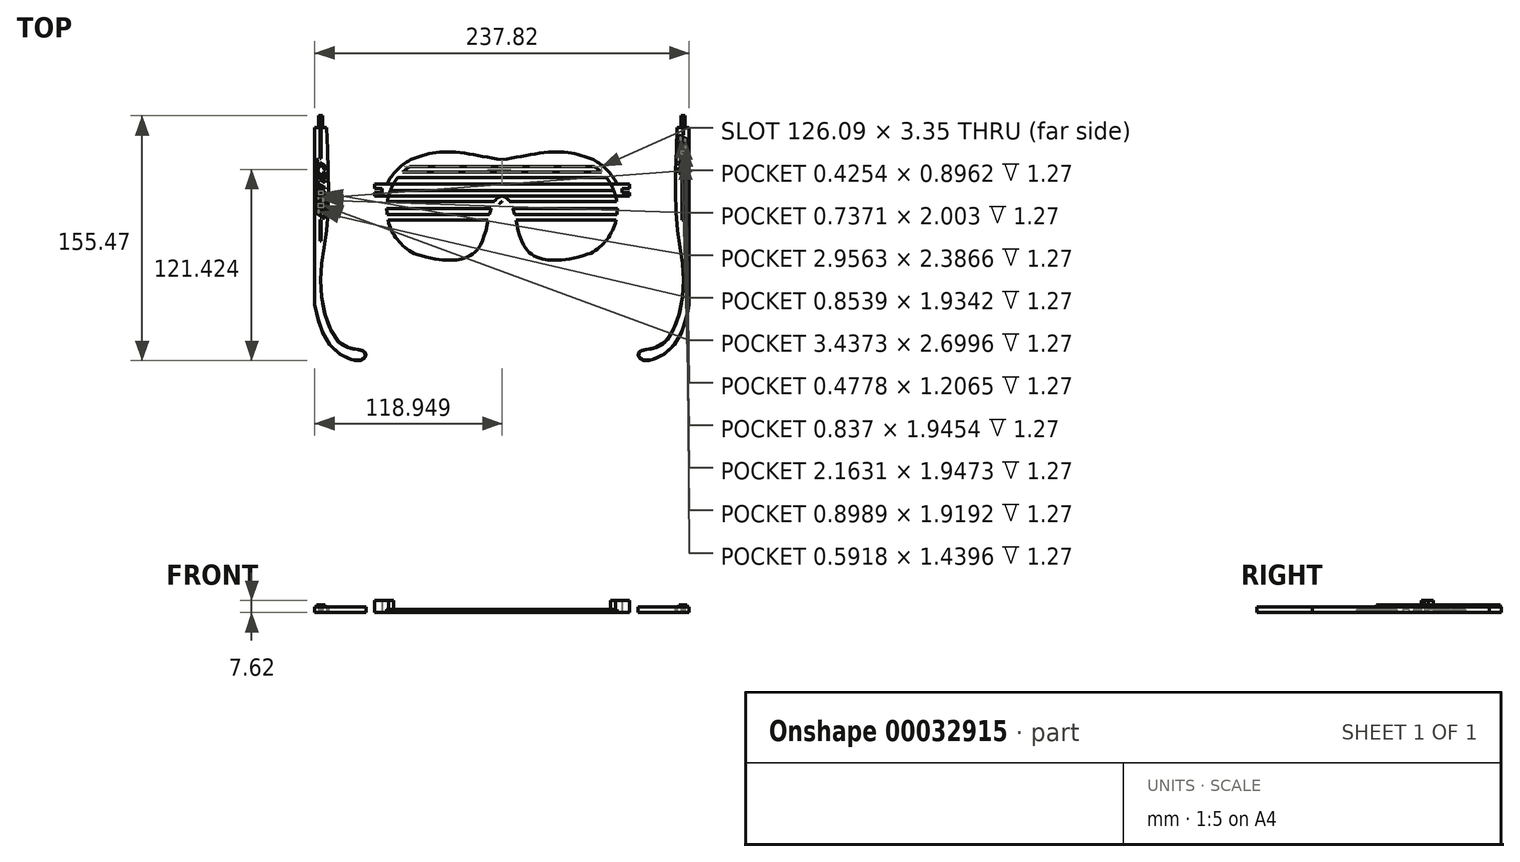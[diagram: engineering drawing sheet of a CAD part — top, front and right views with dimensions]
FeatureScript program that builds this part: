
annotation { "Feature Type Name" : "Feature", "Feature Type Description" : "" }
export const myFeature = defineFeature(function(context is Context, id is Id, definition is map)
    precondition{}
    {
        {
            var Q0;
            Q0=qCreatedBy(makeId("Top.planeOp"),FACE);
            var sketch = newSketch(context, id + "F0", { "sketchPlane" : qUnion([Q0])});
            skArc(sketch, "E0", {"start": v(-58.18, 23.09) * mm, "mid": v(-66.75, 16.58) * mm, "end": v(-72.97, 7.79) * mm});
            skFitSpline(sketch, "E1", {"points": [v(-57.43, -39.6) * mm, v(-39.44, -43.85) * mm, v(-13.97, -37.35) * mm, v(-3.73, -9.63) * mm, v(0, -3.56) * mm], "startDerivative": vector(65.92, -21.2) * mm, "endDerivative": vector(30.4, 18.63) * mm});
            skPoint(sketch, "E2.end.orphan", {"position": v(0, 23.09) * mm});
            skFitSpline(sketch, "E3", {"points": [v(-58.18, 23.09) * mm, v(-37.45, 28.08) * mm, v(0, 23.09) * mm], "startDerivative": vector(44.62, 16.02) * mm, "endDerivative": vector(71, -11.96) * mm});
            skFitSpline(sketch, "E4.3", {"points": [v(-56.35, -36.25) * mm, v(-54.97, -36.7) * mm, v(-52.25, -37.57) * mm, v(-48.08, -38.77) * mm, v(-44.4, -39.6) * mm, v(-41.23, -40.1) * mm, v(-38.72, -40.4) * mm, v(-36.07, -40.59) * mm, v(-32.45, -40.66) * mm, v(-27.87, -40.34) * mm, v(-23.61, -39.32) * mm, v(-20.6, -38.03) * mm, v(-18.93, -37.02) * mm, v(-17.7, -36.07) * mm, v(-16.86, -35.3) * mm, v(-16.07, -34.45) * mm, v(-15.07, -33.16) * mm, v(-13.9, -31.3) * mm, v(-12.26, -27.9) * mm, v(-10.6, -23.01) * mm, v(-9.35, -17.93) * mm, v(-8.48, -14.07) * mm, v(-7.85, -11.35) * mm, v(-7.31, -9.28) * mm, v(-6.84, -7.75) * mm, v(-6.33, -6.34) * mm, v(-5.63, -4.75) * mm, v(-4.6, -3.07) * mm, v(-3.35, -1.63) * mm, v(-2.35, -0.87) * mm, v(-1.84, -0.56) * mm]});
            skArc(sketch, "E4.4", {"start": v(-56.62, 19.9) * mm, "mid": v(-73.17, -8.43) * mm, "end": v(-55.97, -36.37) * mm});
            skFitSpline(sketch, "E4.5", {"points": [v(-56.99, 19.77) * mm, v(-55.12, 20.44) * mm, v(-51.46, 21.77) * mm, v(-46.85, 23.15) * mm, v(-43.01, 23.97) * mm, v(-40.53, 24.33) * mm, v(-38.46, 24.5) * mm, v(-36.34, 24.62) * mm, v(-33.53, 24.6) * mm, v(-29.93, 24.38) * mm, v(-24.87, 23.84) * mm, v(-18.1, 22.8) * mm, v(-9.51, 21.2) * mm, v(-3.58, 20.12) * mm, v(-0.58, 19.62) * mm]});
            skLineSegment(sketch, "E5", {"start": v(-1.84, -0.56) * mm, "end": v(0, 0) * mm});
            skArc(sketch, "E6.MirrorCS", {"start": v(56.74, 19.9) * mm, "mid": v(73.22, -8.43) * mm, "end": v(56.09, -36.37) * mm});
            skArc(sketch, "E7.MirrorCS", {"start": v(58.18, 23.09) * mm, "mid": v(66.75, 16.58) * mm, "end": v(72.97, 7.79) * mm});
            skFitSpline(sketch, "E8.MirrorCS", {"points": [v(57.43, -39.6) * mm, v(39.44, -43.85) * mm, v(13.97, -37.35) * mm, v(3.73, -9.63) * mm, v(0, -3.56) * mm], "startDerivative": vector(-65.92, -21.2) * mm, "endDerivative": vector(-30.4, 18.63) * mm});
            skFitSpline(sketch, "E9.MirrorCS", {"points": [v(56.35, -36.26) * mm, v(54.98, -36.7) * mm, v(52.25, -37.59) * mm, v(48.08, -38.79) * mm, v(44.4, -39.61) * mm, v(41.23, -40.12) * mm, v(38.72, -40.41) * mm, v(36.08, -40.6) * mm, v(32.45, -40.68) * mm, v(27.87, -40.36) * mm, v(23.62, -39.34) * mm, v(20.61, -38.04) * mm, v(18.93, -37.03) * mm, v(17.71, -36.09) * mm, v(16.86, -35.31) * mm, v(16.08, -34.46) * mm, v(15.07, -33.18) * mm, v(13.9, -31.32) * mm, v(12.26, -27.9) * mm, v(10.6, -23.03) * mm, v(9.36, -17.94) * mm, v(8.49, -14.08) * mm, v(7.86, -11.37) * mm, v(7.32, -9.3) * mm, v(6.84, -7.77) * mm, v(6.34, -6.36) * mm, v(5.63, -4.76) * mm, v(4.61, -3.08) * mm, v(3.35, -1.64) * mm, v(2.36, -0.89) * mm, v(1.84, -0.57) * mm]});
            skFitSpline(sketch, "E10.MirrorCS", {"points": [v(58.18, 23.09) * mm, v(37.45, 28.08) * mm, v(0, 23.09) * mm], "startDerivative": vector(-44.62, 16.02) * mm, "endDerivative": vector(-71, -11.96) * mm});
            skFitSpline(sketch, "E11.MirrorCS", {"points": [v(56.99, 19.78) * mm, v(55.12, 20.45) * mm, v(51.45, 21.78) * mm, v(46.85, 23.16) * mm, v(43.01, 23.97) * mm, v(40.52, 24.33) * mm, v(38.46, 24.52) * mm, v(36.34, 24.63) * mm, v(33.53, 24.61) * mm, v(29.93, 24.4) * mm, v(24.87, 23.85) * mm, v(18.1, 22.8) * mm, v(9.5, 21.22) * mm, v(3.57, 20.13) * mm, v(0.58, 19.62) * mm]});
            skLineSegment(sketch, "E12.MirrorCS", {"start": v(1.84, -0.56) * mm, "end": v(0, 0) * mm});
            skLineSegment(sketch, "E13", {"start": v(-0.58, 19.62) * mm, "end": v(0.58, 19.62) * mm});
            skFitSpline(sketch, "E14", {"points": [v(-3.73, -9.63) * mm, v(0, -3.56) * mm, v(3.73, -9.63) * mm], "startDerivative": vector(7.46, 18.21) * mm, "endDerivative": vector(7.46, -18.21) * mm});
            skLineSegment(sketch, "E15", {"start": v(0, 0) * mm, "end": v(72.2, 0) * mm});
            skLineSegment(sketch, "E16", {"start": v(0, 0) * mm, "end": v(-72.14, 0) * mm});
            skLineSegment(sketch, "E17", {"start": v(-71.03, 3.44) * mm, "end": v(71.08, 3.44) * mm});
            skLineSegment(sketch, "E18", {"start": v(-68.96, 7.79) * mm, "end": v(69.02, 7.79) * mm});
            skLineSegment(sketch, "E19", {"start": v(66.43, 11.64) * mm, "end": v(-66.36, 11.64) * mm});
            skLineSegment(sketch, "E20", {"start": v(-63, 15.29) * mm, "end": v(63.09, 15.29) * mm});
            skLineSegment(sketch, "E21", {"start": v(-58.73, 18.64) * mm, "end": v(58.83, 18.64) * mm});
            skLineSegment(sketch, "E22", {"start": v(-52.46, 21.38) * mm, "end": v(-10.42, 21.38) * mm});
            skLineSegment(sketch, "E23.trimOffspring", {"start": v(10.37, 21.38) * mm, "end": v(52.48, 21.38) * mm});
            skLineSegment(sketch, "E24.MirrorCS", {"start": v(-71.03, -3.44) * mm, "end": v(-4.8, -3.44) * mm});
            skLineSegment(sketch, "E25.MirrorCS", {"start": v(-68.96, -7.79) * mm, "end": v(-6.84, -7.79) * mm});
            skLineSegment(sketch, "E26.MirrorCS", {"start": v(-63, -15.29) * mm, "end": v(-8.76, -15.29) * mm});
            skLineSegment(sketch, "E27.MirrorCS", {"start": v(-58.73, -18.64) * mm, "end": v(-9.54, -18.64) * mm});
            skLineSegment(sketch, "E28.MirrorCS", {"start": v(-52.46, -21.38) * mm, "end": v(-10.42, -21.38) * mm});
            skLineSegment(sketch, "E29.MirrorCS", {"start": v(10.37, -21.38) * mm, "end": v(52.48, -21.38) * mm});
            skLineSegment(sketch, "E30.trimOffspring", {"start": v(-7.9, -11.64) * mm, "end": v(-66.36, -11.64) * mm});
            skLineSegment(sketch, "E31.trimOffspring", {"start": v(8.76, -15.29) * mm, "end": v(63.09, -15.29) * mm});
            skLineSegment(sketch, "E32.trimOffspring", {"start": v(9.54, -18.64) * mm, "end": v(58.83, -18.64) * mm});
            skLineSegment(sketch, "E33.trimOffspring", {"start": v(6.84, -7.79) * mm, "end": v(69.02, -7.79) * mm});
            skLineSegment(sketch, "E34", {"start": v(-71.03, -3.44) * mm, "end": v(-72.84, -3.44) * mm});
            skLineSegment(sketch, "E35", {"start": v(-68.96, -7.79) * mm, "end": v(-73.17, -7.79) * mm});
            skLineSegment(sketch, "E36", {"start": v(-66.36, -11.64) * mm, "end": v(-72.97, -11.64) * mm});
            skLineSegment(sketch, "E37", {"start": v(-63, -15.29) * mm, "end": v(-72.34, -15.29) * mm});
            skLineSegment(sketch, "E38", {"start": v(-58.73, -18.64) * mm, "end": v(-71.37, -18.64) * mm});
            skLineSegment(sketch, "E39", {"start": v(-52.46, -21.38) * mm, "end": v(-70.26, -21.38) * mm});
            skLineSegment(sketch, "E40.MirrorCS", {"start": v(52.46, -21.38) * mm, "end": v(70.28, -21.38) * mm});
            skLineSegment(sketch, "E41.MirrorCS", {"start": v(58.76, -18.64) * mm, "end": v(71.39, -18.64) * mm});
            skLineSegment(sketch, "E42.MirrorCS", {"start": v(63.03, -15.29) * mm, "end": v(72.36, -15.29) * mm});
            skLineSegment(sketch, "E43.MirrorCS", {"start": v(68.98, -7.79) * mm, "end": v(73.19, -7.79) * mm});
            skLineSegment(sketch, "E44", {"start": v(-66.3, -27.83) * mm, "end": v(-12.33, -27.83) * mm});
            skLineSegment(sketch, "E45", {"start": v(-62.82, -31.58) * mm, "end": v(-14.11, -31.58) * mm});
            skLineSegment(sketch, "E46", {"start": v(-58.53, -34.89) * mm, "end": v(-16.49, -34.89) * mm});
            skLineSegment(sketch, "E47", {"start": v(-50.85, -37.97) * mm, "end": v(-20.6, -37.97) * mm});
            skLineSegment(sketch, "E48.trimOffspring", {"start": v(11.17, -24.56) * mm, "end": v(68.65, -24.54) * mm});
            skLineSegment(sketch, "E49.trimOffspring", {"start": v(12.33, -27.83) * mm, "end": v(66.37, -27.83) * mm});
            skLineSegment(sketch, "E50.trimOffspring", {"start": v(14.1, -31.58) * mm, "end": v(62.9, -31.58) * mm});
            skLineSegment(sketch, "E51.trimOffspring", {"start": v(16.48, -34.89) * mm, "end": v(58.62, -34.89) * mm});
            skLineSegment(sketch, "E52.trimOffspring", {"start": v(20.58, -37.97) * mm, "end": v(50.9, -37.97) * mm});
            skLineSegment(sketch, "E53.trimOffspring", {"start": v(-11.17, -24.56) * mm, "end": v(-68.58, -24.56) * mm});
            skLineSegment(sketch, "E54", {"start": v(-10.42, -21.38) * mm, "end": v(-10.24, -21.38) * mm});
            skLineSegment(sketch, "E55", {"start": v(10.37, 21.38) * mm, "end": v(10.35, 21.38) * mm});
            skLineSegment(sketch, "E56", {"start": v(-10.42, 21.38) * mm, "end": v(-10.4, 21.38) * mm});
            skLineSegment(sketch, "E57", {"start": v(56.07, -36.36) * mm, "end": v(56.09, -36.37) * mm});
            skLineSegment(sketch, "E58", {"start": v(10.37, -21.38) * mm, "end": v(10.24, -21.38) * mm});
            skLineSegment(sketch, "E59", {"start": v(7.91, -11.64) * mm, "end": v(7.9, -11.64) * mm});
            skLineSegment(sketch, "E60", {"start": v(6.84, -7.79) * mm, "end": v(6.82, -7.79) * mm});
            skLineSegment(sketch, "E61", {"start": v(4.8, -3.44) * mm, "end": v(4.78, -3.44) * mm});
            skLineSegment(sketch, "E62", {"start": v(70.28, -21.38) * mm, "end": v(70.34, -21.38) * mm});
            skLineSegment(sketch, "E63", {"start": v(71.39, -18.64) * mm, "end": v(71.43, -18.64) * mm});
            skLineSegment(sketch, "E64", {"start": v(72.36, -15.29) * mm, "end": v(72.41, -15.29) * mm});
            skLineSegment(sketch, "E65", {"start": v(73, -11.63) * mm, "end": v(73, -11.63) * mm});
            skLineSegment(sketch, "E66", {"start": v(73.19, -7.79) * mm, "end": v(73.24, -7.79) * mm});
            skLineSegment(sketch, "E67", {"start": v(66.43, -11.64) * mm, "end": v(66.4, -11.63) * mm});
            skLineSegment(sketch, "E68", {"start": v(56.73, 19.88) * mm, "end": v(56.74, 19.9) * mm});
            skLineSegment(sketch, "E69", {"start": v(1.84, -0.56) * mm, "end": v(1.84, -0.57) * mm});
            skLineSegment(sketch, "E70", {"start": v(71.05, -3.43) * mm, "end": v(71.08, -3.44) * mm});
            skLineSegment(sketch, "E71", {"start": v(8.76, -15.29) * mm, "end": v(8.75, -15.29) * mm});
            skLineSegment(sketch, "E72", {"start": v(72.85, -3.43) * mm, "end": v(72.86, -3.43) * mm});
            skLineSegment(sketch, "E73", {"start": v(4.8, -3.44) * mm, "end": v(72.89, -3.43) * mm});
            skPoint(sketch, "E74", {"position": v(72.86, -3.43) * mm});
            skPoint(sketch, "E75.trimOffspring.end.orphan", {"position": v(83.8, -3.43) * mm});
            skLineSegment(sketch, "E76", {"start": v(7.91, -11.64) * mm, "end": v(73.02, -11.64) * mm});
            skPoint(sketch, "E77", {"position": v(73, -11.63) * mm});
            skLineSegment(sketch, "E78", {"start": v(-75.78, 0) * mm, "end": v(-81.03, 0) * mm});
            skLineSegment(sketch, "E79", {"start": v(-72.97, 7.79) * mm, "end": v(-81.03, 7.79) * mm});
            skLineSegment(sketch, "E80", {"start": v(75.78, 0) * mm, "end": v(81.08, 0) * mm});
            skLineSegment(sketch, "E81", {"start": v(72.97, 7.79) * mm, "end": v(81.08, 7.79) * mm});
            skLineSegment(sketch, "E82", {"start": v(81.08, 7.79) * mm, "end": v(81.08, 4.74) * mm});
            skLineSegment(sketch, "E83", {"start": v(-81.03, 0) * mm, "end": v(-81.03, 2.2) * mm});
            skLineSegment(sketch, "E84.rect.bottom", {"start": v(-76.1, 2.2) * mm, "end": v(-81.03, 2.2) * mm});
            skLineSegment(sketch, "E84.rect.top", {"start": v(-76.1, 4.74) * mm, "end": v(-81.03, 4.74) * mm});
            skLineSegment(sketch, "E84.rect.left", {"start": v(-76.1, 2.2) * mm, "end": v(-76.1, 4.74) * mm});
            skPoint(sketch, "E84.rect.middle", {"position": v(-81.03, 3.9) * mm});
            skLineSegment(sketch, "E85.trimOffspring", {"start": v(-81.03, 4.74) * mm, "end": v(-81.03, 7.79) * mm});
            skPoint(sketch, "E86.startSnap0", {"position": v(0.04, 15.29) * mm});
            skLineSegment(sketch, "E87.MirrorCS", {"start": v(76.18, 4.74) * mm, "end": v(81.1, 4.74) * mm});
            skLineSegment(sketch, "E88.MirrorCS", {"start": v(76.18, 2.2) * mm, "end": v(76.18, 4.74) * mm});
            skLineSegment(sketch, "E89.MirrorCS", {"start": v(76.18, 2.2) * mm, "end": v(81.1, 2.2) * mm});
            skLineSegment(sketch, "E90.trimOffspring", {"start": v(81.08, 2.2) * mm, "end": v(81.08, 0) * mm});
            skArc(sketch, "E91.trimOffspring", {"start": v(-75.78, 0) * mm, "mid": v(-73.43, -22.96) * mm, "end": v(-57.43, -39.6) * mm});
            skArc(sketch, "E92.trimOffspring", {"start": v(75.78, 0) * mm, "mid": v(73.43, -22.96) * mm, "end": v(57.43, -39.6) * mm});
            skLineSegment(sketch, "E93", {"start": v(-72.97, 7.79) * mm, "end": v(-68.96, 7.79) * mm});
            skLineSegment(sketch, "E94", {"start": v(-75.78, 0) * mm, "end": v(-72.14, 0) * mm});
            skLineSegment(sketch, "E95", {"start": v(75.78, 0) * mm, "end": v(72.2, 0) * mm});
            skLineSegment(sketch, "E96", {"start": v(72.97, 7.79) * mm, "end": v(69.02, 7.79) * mm});
            skSolve(sketch);
        }
        {
            var Q0;
            Q0=makeQuery(id+"F0.imprint","IMPRINT",FACE,{"disambiguationData":[TD([[makeQuery(id+"F0.imprint","IMPRINT",EDGE,{"derivedFrom":sQuery(id+"F0.wireOp",EDGE,"E0")}),1.0]])]});
            var Q1;
            {var subQ1=sQuery(id+"F0.wireOp",EDGE,"E19");Q1=makeQuery(id+"F0.imprint","IMPRINT",FACE,{"disambiguationData":[TD([[makeQuery(id+"F0.imprint","IMPRINT",EDGE,{"derivedFrom":subQ1}),-1.0]])]});}
            var Q2;
            {var subQ2=sQuery(id+"F0.wireOp",EDGE,"E13");Q2=makeQuery(id+"F0.imprint","IMPRINT",FACE,{"disambiguationData":[TD([[makeQuery(id+"F0.imprint","IMPRINT",EDGE,{"derivedFrom":subQ2}),-1.0]])]});}
            var Q3;
            {var subQ1=sQuery(id+"F0.wireOp",EDGE,"E17");Q3=makeQuery(id+"F0.imprint","IMPRINT",FACE,{"disambiguationData":[TD([[makeQuery(id+"F0.imprint","IMPRINT",EDGE,{"derivedFrom":subQ1}),1.0]])]});}
            var Q4;
            {var subQ3=sQuery(id+"F0.wireOp",EDGE,"E5");Q4=makeQuery(id+"F0.imprint","IMPRINT",FACE,{"disambiguationData":[TD([[makeQuery(id+"F0.imprint","IMPRINT",EDGE,{"derivedFrom":subQ3}),1.0]])]});}
            var Q5;
            Q5=makeQuery(id+"F0.imprint","IMPRINT",FACE,{"disambiguationData":[TD([[makeQuery(id+"F0.imprint","IMPRINT",EDGE,{"derivedFrom":sQuery(id+"F0.wireOp",EDGE,"E12.MirrorCS")}),-1.0]])]});
            var Q6;
            {var subQ11=sQuery(id+"F0.wireOp",EDGE,"E33.trimOffspring");Q6=makeQuery(id+"F0.imprint","IMPRINT",FACE,{"disambiguationData":[TD([[makeQuery(id+"F0.imprint","IMPRINT",EDGE,{"derivedFrom":subQ11}),-1.0]])]});}
            var Q7;
            {var subQ2=sQuery(id+"F0.wireOp",EDGE,"E25.MirrorCS");Q7=makeQuery(id+"F0.imprint","IMPRINT",FACE,{"disambiguationData":[TD([[makeQuery(id+"F0.imprint","IMPRINT",EDGE,{"derivedFrom":subQ2}),-1.0]])]});}
            var Q8;
            {var subQ3=sQuery(id+"F0.wireOp",EDGE,"E26.MirrorCS");Q8=makeQuery(id+"F0.imprint","IMPRINT",FACE,{"disambiguationData":[TD([[makeQuery(id+"F0.imprint","IMPRINT",EDGE,{"derivedFrom":subQ3}),-1.0]])]});}
            var Q9;
            {var subQ10=sQuery(id+"F0.wireOp",EDGE,"E31.trimOffspring");Q9=makeQuery(id+"F0.imprint","IMPRINT",FACE,{"disambiguationData":[TD([[makeQuery(id+"F0.imprint","IMPRINT",EDGE,{"derivedFrom":subQ10}),-1.0]])]});}
            var Q10;
            {var subQ7=sQuery(id+"F0.wireOp",EDGE,"E29.MirrorCS");Q10=makeQuery(id+"F0.imprint","IMPRINT",FACE,{"disambiguationData":[TD([[makeQuery(id+"F0.imprint","IMPRINT",EDGE,{"derivedFrom":subQ7}),-1.0]])]});}
            var Q11;
            Q11=makeQuery(id+"F0.imprint","IMPRINT",FACE,{"disambiguationData":[TD([[makeQuery(id+"F0.imprint","IMPRINT",EDGE,{"derivedFrom":sQuery(id+"F0.wireOp",EDGE,"E28.MirrorCS")}),-1.0]])]});
            var Q12;
            {var subQ1=sQuery(id+"F0.wireOp",EDGE,"E44");Q12=makeQuery(id+"F0.imprint","IMPRINT",FACE,{"disambiguationData":[TD([[makeQuery(id+"F0.imprint","IMPRINT",EDGE,{"derivedFrom":subQ1}),-1.0]])]});}
            var Q13;
            {var subQ1=sQuery(id+"F0.wireOp",EDGE,"E49.trimOffspring");Q13=makeQuery(id+"F0.imprint","IMPRINT",FACE,{"disambiguationData":[TD([[makeQuery(id+"F0.imprint","IMPRINT",EDGE,{"derivedFrom":subQ1}),-1.0]])]});}
            var Q14;
            {var subQ2=sQuery(id+"F0.wireOp",EDGE,"E51.trimOffspring");Q14=makeQuery(id+"F0.imprint","IMPRINT",FACE,{"disambiguationData":[TD([[makeQuery(id+"F0.imprint","IMPRINT",EDGE,{"derivedFrom":subQ2}),-1.0]])]});}
            var Q15;
            {var subQ1=sQuery(id+"F0.wireOp",EDGE,"E46");Q15=makeQuery(id+"F0.imprint","IMPRINT",FACE,{"disambiguationData":[TD([[makeQuery(id+"F0.imprint","IMPRINT",EDGE,{"derivedFrom":subQ1}),-1.0]])]});}
            var Q16;
            Q16=makeQuery(id+"F0.imprint","IMPRINT",FACE,{"disambiguationData":[TD([[makeQuery(id+"F0.imprint","IMPRINT",EDGE,{"derivedFrom":sQuery(id+"F0.wireOp",EDGE,"E1")}),1.0]])]});
            var Q17;
            Q17=makeQuery(id+"F0.imprint","IMPRINT",FACE,{"disambiguationData":[TD([[makeQuery(id+"F0.imprint","IMPRINT",EDGE,{"derivedFrom":sQuery(id+"F0.wireOp",EDGE,"E78")}),-1.0]])]});
            var Q18;
            Q18=makeQuery(id+"F0.imprint","IMPRINT",FACE,{"disambiguationData":[TD([[makeQuery(id+"F0.imprint","IMPRINT",EDGE,{"derivedFrom":sQuery(id+"F0.wireOp",EDGE,"E80")}),1.0]])]});
            extrude(context, id + "F1", {"entities" : qUnion([Q0, Q1, Q2, Q3, Q4, Q5, Q6, Q7, Q8, Q9, Q10, Q11, Q12, Q13, Q14, Q15, Q16, Q17, Q18]), "depth" : 1.9 * mm});
        }
        {
            var Q0;
            Q0=qCreatedBy(makeId("Top.planeOp"),FACE);
            var sketch = newSketch(context, id + "F2", { "sketchPlane" : qUnion([Q0])});
            skLineSegment(sketch, "E97", {"start": v(-118.9, 43.4) * mm, "end": v(-118.9, -68.92) * mm});
            skLineSegment(sketch, "E98", {"start": v(-118.9, 43.4) * mm, "end": v(-116.37, 43.4) * mm});
            skPoint(sketch, "E99.2.internal.snap0", {"position": v(-115.1, 43.4) * mm});
            skFitSpline(sketch, "E99", {"points": [v(-111.29, 43.4) * mm, v(-111.29, -19.18) * mm, v(-115.1, -60.4) * mm, v(-101.96, -94.17) * mm, v(-89.37, -97.9) * mm, v(-86.4, -100.45) * mm, v(-89.74, -104.24) * mm, v(-108.09, -95.9) * mm, v(-118.9, -68.92) * mm], "startDerivative": vector(13.53, -320.53) * mm, "endDerivative": vector(-45.53, 212.03) * mm});
            skPoint(sketch, "E100.orphan", {"position": v(-118.9, -83.6) * mm});
            skFitSpline(sketch, "E101.MirrorCS", {"points": [v(111.29, 43.4) * mm, v(111.29, -19.18) * mm, v(115.1, -60.4) * mm, v(101.96, -94.17) * mm, v(89.37, -97.9) * mm, v(86.4, -100.45) * mm, v(89.74, -104.24) * mm, v(108.09, -95.9) * mm, v(118.9, -68.92) * mm], "startDerivative": vector(-13.53, -320.53) * mm, "endDerivative": vector(45.53, 212.03) * mm});
            skLineSegment(sketch, "E102.MirrorCS", {"start": v(118.9, 43.4) * mm, "end": v(118.9, -68.92) * mm});
            skLineSegment(sketch, "E103.MirrorCS", {"start": v(118.9, 43.4) * mm, "end": v(116.37, 43.4) * mm});
            skLineSegment(sketch, "E104.rect.bottom", {"start": v(-116.37, 51.01) * mm, "end": v(-113.83, 51.01) * mm});
            skLineSegment(sketch, "E104.rect.left", {"start": v(-116.37, 51.01) * mm, "end": v(-116.37, 43.4) * mm});
            skLineSegment(sketch, "E104.rect.right", {"start": v(-113.83, 51.01) * mm, "end": v(-113.83, 43.4) * mm});
            skPoint(sketch, "E104.rect.top.end.orphan", {"position": v(-113.83, 35.77) * mm});
            skPoint(sketch, "E105.orphan", {"position": v(-116.37, 35.77) * mm});
            skLineSegment(sketch, "E106.trimOffspring", {"start": v(-113.83, 43.4) * mm, "end": v(-111.29, 43.4) * mm});
            skLineSegment(sketch, "E107.MirrorCS", {"start": v(116.37, 51.01) * mm, "end": v(116.37, 43.4) * mm});
            skLineSegment(sketch, "E108.MirrorCS", {"start": v(116.37, 51.01) * mm, "end": v(113.83, 51.01) * mm});
            skLineSegment(sketch, "E109.MirrorCS", {"start": v(113.83, 51.01) * mm, "end": v(113.83, 43.4) * mm});
            skLineSegment(sketch, "E110.trimOffspring", {"start": v(113.83, 43.4) * mm, "end": v(111.29, 43.4) * mm});
            skSolve(sketch);
        }
        {
            var Q0;
            Q0=makeQuery(id+"F0.imprint","IMPRINT",FACE,{"disambiguationData":[TD([[makeQuery(id+"F0.imprint","IMPRINT",EDGE,{"derivedFrom":sQuery(id+"F0.wireOp",EDGE,"E78")}),-1.0]])]});
            var Q1;
            Q1=makeQuery(id+"F0.imprint","IMPRINT",FACE,{"disambiguationData":[TD([[makeQuery(id+"F0.imprint","IMPRINT",EDGE,{"derivedFrom":sQuery(id+"F0.wireOp",EDGE,"E80")}),1.0]])]});
            extrude(context, id + "F3", {"entities" : qUnion([Q0, Q1]), "operationType" : NewBodyOperationType.ADD, "depth" : 7.62 * mm});
        }
        {
            var Q0;
            Q0=makeQuery(id+"F2.imprint","IMPRINT",FACE,{"disambiguationData":[TD([[makeQuery(id+"F2.imprint","IMPRINT",EDGE,{"derivedFrom":sQuery(id+"F2.wireOp",EDGE,"E97")}),1.0]])]});
            var Q1;
            Q1=makeQuery(id+"F2.imprint","IMPRINT",FACE,{"disambiguationData":[TD([[makeQuery(id+"F2.imprint","IMPRINT",EDGE,{"derivedFrom":sQuery(id+"F2.wireOp",EDGE,"E101.MirrorCS")}),1.0]])]});
            extrude(context, id + "F4", {"entities" : qUnion([Q0, Q1]), "depth" : 4.93 * mm});
        }
        {
            var Q0;
            Q0=makeQuery(id+"F4.opExtrude","CAP_FACE",FACE,{"disambiguationData":[OSD([sQuery(id+"F2.wireOp",EDGE,"E97"),sQuery(id+"F2.wireOp",EDGE,"E98"),sQuery(id+"F2.wireOp",EDGE,"E99"),sQuery(id+"F2.wireOp",EDGE,"E104.rect.bottom"),sQuery(id+"F2.wireOp",EDGE,"E104.rect.left"),sQuery(id+"F2.wireOp",EDGE,"E104.rect.right"),sQuery(id+"F2.wireOp",EDGE,"E106.trimOffspring")])],"isStart":false});
            var sketch = newSketch(context, id + "F5", { "sketchPlane" : qUnion([Q0])});
            skLineSegment(sketch, "E111", {"start": v(-117.84, -10.83) * mm, "end": v(-117.84, -7.26) * mm});
            skLineSegment(sketch, "E112", {"start": v(-112.42, -14.1) * mm, "end": v(-112.42, -11.99) * mm});
            skLineSegment(sketch, "E113", {"start": v(-117.84, -10.83) * mm, "end": v(-112.42, -14.1) * mm});
            skLineSegment(sketch, "E114", {"start": v(-117.84, -7.26) * mm, "end": v(-115.14, -8.88) * mm});
            skLineSegment(sketch, "E115", {"start": v(-115.14, -8.88) * mm, "end": v(-115.14, -10.8) * mm});
            skLineSegment(sketch, "E116", {"start": v(-115.14, -10.8) * mm, "end": v(-112.42, -9) * mm});
            skLineSegment(sketch, "E117", {"start": v(-112.42, -9) * mm, "end": v(-112.42, -10.6) * mm});
            skLineSegment(sketch, "E118", {"start": v(-112.42, -10.6) * mm, "end": v(-113.53, -11.32) * mm});
            skLineSegment(sketch, "E119", {"start": v(-113.53, -11.32) * mm, "end": v(-112.42, -11.99) * mm});
            skLineSegment(sketch, "E120", {"start": v(-112.42, -11.99) * mm, "end": v(-112.42, -14.1) * mm});
            skLineSegment(sketch, "E121", {"start": v(-112.42, -9.01) * mm, "end": v(-117.84, -5.74) * mm});
            skLineSegment(sketch, "E122", {"start": v(-117.84, -5.74) * mm, "end": v(-117.84, -2.81) * mm});
            skLineSegment(sketch, "E123", {"start": v(-117.84, -2.81) * mm, "end": v(-112.42, -6.08) * mm});
            skLineSegment(sketch, "E124", {"start": v(-112.42, -6.08) * mm, "end": v(-112.42, -9.01) * mm});
            skLineSegment(sketch, "E125", {"start": v(-112.42, -5.42) * mm, "end": v(-117.84, -2.15) * mm});
            skLineSegment(sketch, "E126", {"start": v(-117.84, -2.15) * mm, "end": v(-117.84, 0.92) * mm});
            skLineSegment(sketch, "E127", {"start": v(-117.84, 0.92) * mm, "end": v(-115.33, -0.6) * mm});
            skLineSegment(sketch, "E128", {"start": v(-115.33, -0.6) * mm, "end": v(-115.33, -2.21) * mm});
            skLineSegment(sketch, "E129", {"start": v(-115.33, -2.21) * mm, "end": v(-114.94, -2.45) * mm});
            skLineSegment(sketch, "E130", {"start": v(-114.94, -2.45) * mm, "end": v(-114.94, 0) * mm});
            skLineSegment(sketch, "E131", {"start": v(-114.94, 0) * mm, "end": v(-112.42, -1.52) * mm});
            skLineSegment(sketch, "E132", {"start": v(-112.42, -1.52) * mm, "end": v(-112.42, -5.42) * mm});
            skLineSegment(sketch, "E133", {"start": v(-117.84, 2.04) * mm, "end": v(-112.42, -1.22) * mm});
            skLineSegment(sketch, "E134", {"start": v(-112.42, -1.22) * mm, "end": v(-112.42, 1.27) * mm});
            skLineSegment(sketch, "E135", {"start": v(-117.84, 4.54) * mm, "end": v(-117.84, 2.04) * mm});
            skLineSegment(sketch, "E136", {"start": v(-117.84, 5.51) * mm, "end": v(-112.42, 2.25) * mm});
            skLineSegment(sketch, "E137", {"start": v(-112.42, 1.27) * mm, "end": v(-112.42, 2.25) * mm});
            skLineSegment(sketch, "E138", {"start": v(-117.84, 4.54) * mm, "end": v(-117.84, 5.51) * mm});
            skLineSegment(sketch, "E139", {"start": v(-112.42, 4.5) * mm, "end": v(-116.95, 7.23) * mm});
            skLineSegment(sketch, "E140", {"start": v(-116.95, 7.23) * mm, "end": v(-116.95, 5.26) * mm});
            skLineSegment(sketch, "E141", {"start": v(-116.95, 5.26) * mm, "end": v(-117.84, 5.8) * mm});
            skLineSegment(sketch, "E142", {"start": v(-117.84, 5.8) * mm, "end": v(-117.84, 10.32) * mm});
            skLineSegment(sketch, "E143", {"start": v(-116.95, 8.1) * mm, "end": v(-116.95, 9.79) * mm});
            skLineSegment(sketch, "E144", {"start": v(-117.84, 10.32) * mm, "end": v(-116.95, 9.79) * mm});
            skLineSegment(sketch, "E145", {"start": v(-116.95, 8.1) * mm, "end": v(-112.42, 5.38) * mm});
            skLineSegment(sketch, "E146", {"start": v(-112.42, 5.38) * mm, "end": v(-112.42, 4.5) * mm});
            skLineSegment(sketch, "E147", {"start": v(-117.84, 11.14) * mm, "end": v(-116.93, 10.6) * mm});
            skLineSegment(sketch, "E148", {"start": v(-116.93, 10.6) * mm, "end": v(-116.93, 12.55) * mm});
            skLineSegment(sketch, "E149", {"start": v(-116.93, 12.55) * mm, "end": v(-117.84, 13.1) * mm});
            skLineSegment(sketch, "E150", {"start": v(-117.84, 13.1) * mm, "end": v(-117.84, 11.14) * mm});
            skLineSegment(sketch, "E151", {"start": v(-112.42, 9.98) * mm, "end": v(-115.47, 11.82) * mm});
            skLineSegment(sketch, "E152", {"start": v(-112.42, 11.16) * mm, "end": v(-112.42, 10.88) * mm});
            skLineSegment(sketch, "E153", {"start": v(-115.47, 11.82) * mm, "end": v(-115.47, 10.48) * mm});
            skLineSegment(sketch, "E154", {"start": v(-115.47, 10.48) * mm, "end": v(-112.42, 8.64) * mm});
            skLineSegment(sketch, "E155", {"start": v(-112.42, 8.64) * mm, "end": v(-112.42, 9.98) * mm});
            skLineSegment(sketch, "E156", {"start": v(-117.84, 14.15) * mm, "end": v(-112.42, 10.88) * mm});
            skLineSegment(sketch, "E157", {"start": v(-112.42, 10.88) * mm, "end": v(-112.42, 15.19) * mm});
            skLineSegment(sketch, "E158", {"start": v(-112.42, 15.19) * mm, "end": v(-113.17, 15.64) * mm});
            skLineSegment(sketch, "E159", {"start": v(-113.17, 15.64) * mm, "end": v(-113.17, 12.5) * mm});
            skLineSegment(sketch, "E160", {"start": v(-113.17, 12.5) * mm, "end": v(-116.93, 14.76) * mm});
            skLineSegment(sketch, "E161", {"start": v(-117.84, 18.45) * mm, "end": v(-117.84, 14.15) * mm});
            skLineSegment(sketch, "E162", {"start": v(-116.93, 14.76) * mm, "end": v(-116.93, 17.9) * mm});
            skLineSegment(sketch, "E163.trimOffspring", {"start": v(-116.93, 17.9) * mm, "end": v(-117.84, 18.45) * mm});
            skLineSegment(sketch, "E164", {"start": v(-117.84, 19.8) * mm, "end": v(-115.13, 18.18) * mm});
            skLineSegment(sketch, "E165", {"start": v(-113.4, 17.13) * mm, "end": v(-113.4, 19.02) * mm});
            skLineSegment(sketch, "E166", {"start": v(-116.99, 23.09) * mm, "end": v(-117.84, 23.6) * mm});
            skLineSegment(sketch, "E167", {"start": v(-117.84, 23.6) * mm, "end": v(-117.84, 19.8) * mm});
            skLineSegment(sketch, "E168", {"start": v(-116.99, 23.09) * mm, "end": v(-116.99, 20.43) * mm});
            skLineSegment(sketch, "E169", {"start": v(-116.99, 20.43) * mm, "end": v(-115.52, 19.55) * mm});
            skLineSegment(sketch, "E170", {"start": v(-115.52, 19.55) * mm, "end": v(-115.52, 21.36) * mm});
            skLineSegment(sketch, "E171", {"start": v(-115.52, 21.36) * mm, "end": v(-113.4, 20.08) * mm});
            skLineSegment(sketch, "E172", {"start": v(-115.13, 18.18) * mm, "end": v(-115.13, 20.07) * mm});
            skLineSegment(sketch, "E173", {"start": v(-115.13, 20.07) * mm, "end": v(-113.4, 19.02) * mm});
            skLineSegment(sketch, "E174", {"start": v(-113.4, 20.08) * mm, "end": v(-112.42, 19.5) * mm});
            skPoint(sketch, "E175.trimOffspring.end.orphan", {"position": v(-113.4, 20.92) * mm});
            skLineSegment(sketch, "E176.trimOffspring", {"start": v(-113.4, 17.13) * mm, "end": v(-112.42, 16.54) * mm});
            skPoint(sketch, "E177.firstSnap0", {"position": v(-115.52, 20.46) * mm});
            skLineSegment(sketch, "E177.bottom", {"start": v(-115.52, 23.96) * mm, "end": v(-114.84, 23.96) * mm});
            skLineSegment(sketch, "E177.top", {"start": v(-115.52, 50.25) * mm, "end": v(-114.84, 50.25) * mm});
            skLineSegment(sketch, "E177.left", {"start": v(-115.52, 23.96) * mm, "end": v(-115.52, 50.25) * mm});
            skLineSegment(sketch, "E177.right", {"start": v(-114.84, 23.96) * mm, "end": v(-114.84, 50.25) * mm});
            skLineSegment(sketch, "E178.bottom", {"start": v(-114.97, -28.57) * mm, "end": v(-115.56, -28.57) * mm});
            skLineSegment(sketch, "E178.top", {"start": v(-114.97, -14.76) * mm, "end": v(-115.56, -14.76) * mm});
            skLineSegment(sketch, "E178.left", {"start": v(-114.97, -28.57) * mm, "end": v(-114.97, -14.76) * mm});
            skLineSegment(sketch, "E178.right", {"start": v(-115.56, -28.57) * mm, "end": v(-115.56, -14.76) * mm});
            skLineSegment(sketch, "E179.trimOffspring", {"start": v(-112.42, -10.6) * mm, "end": v(-112.42, -6.08) * mm});
            skLineSegment(sketch, "E180.trimOffspring", {"start": v(-117.84, 2.04) * mm, "end": v(-117.84, 4.54) * mm});
            skLineSegment(sketch, "E181.trimOffspring", {"start": v(-117.84, 14.15) * mm, "end": v(-117.84, 18.45) * mm});
            skLineSegment(sketch, "E182.trimOffspring", {"start": v(-117.84, 19.8) * mm, "end": v(-117.84, 23.6) * mm});
            skLineSegment(sketch, "E183.trimOffspring", {"start": v(-112.42, 16.54) * mm, "end": v(-112.42, 19.5) * mm});
            skLineSegment(sketch, "E184.trimOffspring", {"start": v(-112.42, 4.5) * mm, "end": v(-112.42, 5.38) * mm});
            skLineSegment(sketch, "E185.trimOffspring", {"start": v(-112.42, -1.22) * mm, "end": v(-112.42, 2.25) * mm});
            skLineSegment(sketch, "E186.trimOffspring", {"start": v(-112.42, -5.42) * mm, "end": v(-112.42, -1.52) * mm});
            skLineSegment(sketch, "E187.trimOffspring", {"start": v(-117.84, 5.8) * mm, "end": v(-117.84, 13.1) * mm});
            skLineSegment(sketch, "E188.0", {"start": v(-116.85, -4.56) * mm, "end": v(-113.41, -6.63) * mm});
            skLineSegment(sketch, "E188.1", {"start": v(-116.85, -5.19) * mm, "end": v(-116.85, -4.56) * mm});
            skLineSegment(sketch, "E188.2", {"start": v(-113.41, -7.26) * mm, "end": v(-116.85, -5.19) * mm});
            skLineSegment(sketch, "E188.3", {"start": v(-113.41, -6.63) * mm, "end": v(-113.41, -7.26) * mm});
            skLineSegment(sketch, "E189.0", {"start": v(-116.06, -9.4) * mm, "end": v(-116.06, -10.8) * mm});
            skLineSegment(sketch, "E189.1", {"start": v(-116.92, -8.89) * mm, "end": v(-116.06, -9.4) * mm});
            skLineSegment(sketch, "E189.2", {"start": v(-116.92, -10.3) * mm, "end": v(-116.92, -8.89) * mm});
            skLineSegment(sketch, "E189.3", {"start": v(-116.92, -10.3) * mm, "end": v(-116.06, -10.82) * mm});
            skLineSegment(sketch, "E190", {"start": v(-116.06, -10.8) * mm, "end": v(-116.06, -10.82) * mm});
            skLineSegment(sketch, "E191.0", {"start": v(-116.37, -1.18) * mm, "end": v(-116.37, -1.82) * mm});
            skLineSegment(sketch, "E191.1", {"start": v(-116.8, -0.93) * mm, "end": v(-116.37, -1.18) * mm});
            skLineSegment(sketch, "E191.2", {"start": v(-116.8, -1.56) * mm, "end": v(-116.8, -0.93) * mm});
            skLineSegment(sketch, "E191.3", {"start": v(-116.37, -1.82) * mm, "end": v(-116.8, -1.56) * mm});
            skLineSegment(sketch, "E192.1", {"start": v(-114.05, -1.57) * mm, "end": v(-113.31, -2.02) * mm});
            skLineSegment(sketch, "E192.2", {"start": v(-114.05, -2.45) * mm, "end": v(-114.05, -1.57) * mm});
            skLineSegment(sketch, "E193", {"start": v(-114.05, -2.45) * mm, "end": v(-114.05, -3.14) * mm});
            skLineSegment(sketch, "E194", {"start": v(-114.05, -3.14) * mm, "end": v(-113.32, -3.58) * mm});
            skLineSegment(sketch, "E195.trimOffspring", {"start": v(-113.32, -3.58) * mm, "end": v(-113.31, -2.02) * mm});
            skLineSegment(sketch, "E196.0", {"start": v(-116.6, 2.73) * mm, "end": v(-113.65, 0.95) * mm});
            skLineSegment(sketch, "E196.1", {"start": v(-116.6, 2.73) * mm, "end": v(-116.6, 3.34) * mm});
            skLineSegment(sketch, "E196.2", {"start": v(-116.6, 3.34) * mm, "end": v(-113.65, 1.55) * mm});
            skLineSegment(sketch, "E196.3", {"start": v(-113.65, 0.95) * mm, "end": v(-113.65, 1.55) * mm});
            skSolve(sketch);
        }
        {
            var Q0;
            Q0=makeQuery(id+"F5.imprint","IMPRINT",FACE,{"disambiguationData":[TD([[makeQuery(id+"F5.imprint","IMPRINT",EDGE,{"derivedFrom":sQuery(id+"F5.wireOp",EDGE,"E113")}),-1.0]])]});
            var Q1;
            Q1=makeQuery(id+"F5.imprint","IMPRINT",FACE,{"disambiguationData":[TD([[makeQuery(id+"F5.imprint","IMPRINT",EDGE,{"derivedFrom":sQuery(id+"F5.wireOp",EDGE,"E189.0")}),-1.0]])]});
            var Q2;
            Q2=makeQuery(id+"F5.imprint","IMPRINT",FACE,{"disambiguationData":[TD([[makeQuery(id+"F5.imprint","IMPRINT",EDGE,{"derivedFrom":sQuery(id+"F5.wireOp",EDGE,"E188.0")}),-1.0]])]});
            var Q3;
            Q3=makeQuery(id+"F5.imprint","IMPRINT",FACE,{"disambiguationData":[TD([[makeQuery(id+"F5.imprint","IMPRINT",EDGE,{"derivedFrom":sQuery(id+"F5.wireOp",EDGE,"E191.0")}),-1.0]])]});
            var Q4;
            Q4=makeQuery(id+"F5.imprint","IMPRINT",FACE,{"disambiguationData":[TD([[makeQuery(id+"F5.imprint","IMPRINT",EDGE,{"derivedFrom":sQuery(id+"F5.wireOp",EDGE,"E192.1")}),-1.0]])]});
            var Q5;
            Q5=makeQuery(id+"F5.imprint","IMPRINT",FACE,{"disambiguationData":[TD([[makeQuery(id+"F5.imprint","IMPRINT",EDGE,{"derivedFrom":sQuery(id+"F5.wireOp",EDGE,"E196.0")}),1.0]])]});
            extrude(context, id + "F6", {"entities" : qUnion([Q0, Q1, Q2, Q3, Q4, Q5]), "operationType" : NewBodyOperationType.REMOVE, "oppositeDirection" : true, "depth" : 1.27 * mm});
        }
        {
            var Q0;
            Q0=makeQuery(id+"F4.opExtrude","CAP_FACE",FACE,{"disambiguationData":[OSD([sQuery(id+"F2.wireOp",EDGE,"E101.MirrorCS"),sQuery(id+"F2.wireOp",EDGE,"E102.MirrorCS"),sQuery(id+"F2.wireOp",EDGE,"E103.MirrorCS"),sQuery(id+"F2.wireOp",EDGE,"E107.MirrorCS"),sQuery(id+"F2.wireOp",EDGE,"E108.MirrorCS"),sQuery(id+"F2.wireOp",EDGE,"E109.MirrorCS"),sQuery(id+"F2.wireOp",EDGE,"E110.trimOffspring")])],"isStart":false});
            var sketch = newSketch(context, id + "F7", { "sketchPlane" : qUnion([Q0])});
            skPoint(sketch, "E197.startSnap0", {"position": v(117.64, 43.4) * mm});
            skLineSegment(sketch, "E198", {"start": v(112.56, 38.93) * mm, "end": v(112.56, 35.32) * mm});
            skPoint(sketch, "E198.startSnap0", {"position": v(112.56, 43.4) * mm});
            skLineSegment(sketch, "E199", {"start": v(117.64, 36.1) * mm, "end": v(112.56, 38.93) * mm});
            skLineSegment(sketch, "E200", {"start": v(112.56, 35.32) * mm, "end": v(114.71, 34.12) * mm});
            skLineSegment(sketch, "E201", {"start": v(114.71, 34.12) * mm, "end": v(114.71, 36.43) * mm});
            skLineSegment(sketch, "E202", {"start": v(114.71, 36.43) * mm, "end": v(115.14, 36.19) * mm});
            skLineSegment(sketch, "E203", {"start": v(115.14, 36.19) * mm, "end": v(115.14, 34.78) * mm});
            skLineSegment(sketch, "E204", {"start": v(115.14, 34.78) * mm, "end": v(117.64, 33.4) * mm});
            skLineSegment(sketch, "E205", {"start": v(117.64, 33.4) * mm, "end": v(117.64, 36.1) * mm});
            skLineSegment(sketch, "E206", {"start": v(112.56, 34.62) * mm, "end": v(117.64, 31.78) * mm});
            skLineSegment(sketch, "E207", {"start": v(117.64, 31.78) * mm, "end": v(117.64, 29) * mm});
            skLineSegment(sketch, "E208", {"start": v(117.64, 29) * mm, "end": v(115.15, 30.39) * mm});
            skLineSegment(sketch, "E209", {"start": v(115.15, 30.39) * mm, "end": v(115.15, 32.05) * mm});
            skLineSegment(sketch, "E210", {"start": v(115.15, 32.05) * mm, "end": v(112.56, 30.75) * mm});
            skLineSegment(sketch, "E211", {"start": v(112.56, 30.75) * mm, "end": v(112.56, 31.87) * mm});
            skLineSegment(sketch, "E212", {"start": v(112.56, 31.87) * mm, "end": v(114.15, 32.67) * mm});
            skLineSegment(sketch, "E213", {"start": v(114.15, 32.67) * mm, "end": v(112.56, 33.56) * mm});
            skLineSegment(sketch, "E214", {"start": v(112.56, 33.56) * mm, "end": v(112.56, 34.62) * mm});
            skLineSegment(sketch, "E215", {"start": v(117.64, 27.46) * mm, "end": v(112.56, 30.3) * mm});
            skLineSegment(sketch, "E216", {"start": v(112.56, 30.3) * mm, "end": v(112.56, 27.32) * mm});
            skLineSegment(sketch, "E217", {"start": v(112.56, 27.32) * mm, "end": v(117.64, 24.48) * mm});
            skLineSegment(sketch, "E218", {"start": v(117.64, 24.48) * mm, "end": v(117.64, 27.46) * mm});
            skLineSegment(sketch, "E219", {"start": v(117.64, 23.58) * mm, "end": v(112.56, 26.43) * mm});
            skLineSegment(sketch, "E220", {"start": v(112.56, 26.43) * mm, "end": v(112.56, 25.23) * mm});
            skLineSegment(sketch, "E221", {"start": v(112.56, 25.23) * mm, "end": v(114.67, 24.05) * mm});
            skLineSegment(sketch, "E222", {"start": v(114.67, 24.05) * mm, "end": v(114.67, 21.9) * mm});
            skLineSegment(sketch, "E223", {"start": v(114.67, 21.9) * mm, "end": v(117.64, 20.25) * mm});
            skLineSegment(sketch, "E224", {"start": v(117.64, 20.25) * mm, "end": v(117.64, 23.58) * mm});
            skLineSegment(sketch, "E225", {"start": v(117.64, 19.4) * mm, "end": v(112.56, 22.24) * mm});
            skLineSegment(sketch, "E226", {"start": v(112.56, 22.24) * mm, "end": v(112.56, 21.24) * mm});
            skLineSegment(sketch, "E227", {"start": v(112.56, 21.24) * mm, "end": v(114.48, 20.17) * mm});
            skLineSegment(sketch, "E228", {"start": v(114.48, 20.17) * mm, "end": v(114.48, 19.23) * mm});
            skLineSegment(sketch, "E229", {"start": v(112.56, 19.66) * mm, "end": v(112.56, 19.35) * mm});
            skLineSegment(sketch, "E230", {"start": v(117.64, 15.56) * mm, "end": v(117.64, 17.46) * mm});
            skLineSegment(sketch, "E231", {"start": v(117.64, 17.46) * mm, "end": v(115.6, 18.6) * mm});
            skLineSegment(sketch, "E232", {"start": v(115.6, 18.6) * mm, "end": v(115.6, 19.88) * mm});
            skLineSegment(sketch, "E233", {"start": v(115.6, 19.88) * mm, "end": v(117.64, 18.74) * mm});
            skLineSegment(sketch, "E234", {"start": v(117.64, 18.74) * mm, "end": v(117.64, 19.4) * mm});
            skLineSegment(sketch, "E235.trimOffspring", {"start": v(114.48, 19.23) * mm, "end": v(112.56, 20.3) * mm});
            skLineSegment(sketch, "E236", {"start": v(117.64, 16.51) * mm, "end": v(112.56, 19.35) * mm});
            skLineSegment(sketch, "E237", {"start": v(117.64, 15.56) * mm, "end": v(114.98, 17.05) * mm});
            skLineSegment(sketch, "E238", {"start": v(114.98, 17.05) * mm, "end": v(114.98, 14.4) * mm});
            skLineSegment(sketch, "E239", {"start": v(114.98, 14.4) * mm, "end": v(113.16, 15.42) * mm});
            skLineSegment(sketch, "E240", {"start": v(113.16, 15.42) * mm, "end": v(113.16, 17.94) * mm});
            skLineSegment(sketch, "E241", {"start": v(113.16, 17.94) * mm, "end": v(112.56, 18.27) * mm});
            skLineSegment(sketch, "E242", {"start": v(112.56, 18.27) * mm, "end": v(112.56, 14.77) * mm});
            skLineSegment(sketch, "E243", {"start": v(112.56, 14.77) * mm, "end": v(117.64, 11.93) * mm});
            skLineSegment(sketch, "E244", {"start": v(117.64, 11.93) * mm, "end": v(117.64, 12.92) * mm});
            skLineSegment(sketch, "E245", {"start": v(115.83, 14.34) * mm, "end": v(115.83, 15.8) * mm});
            skLineSegment(sketch, "E246", {"start": v(115.83, 15.8) * mm, "end": v(117.64, 14.78) * mm});
            skLineSegment(sketch, "E247", {"start": v(117.64, 14.78) * mm, "end": v(117.64, 15.56) * mm});
            skLineSegment(sketch, "E248.0", {"start": v(115.94, 35.25) * mm, "end": v(116.42, 34.98) * mm});
            skLineSegment(sketch, "E248.1", {"start": v(115.94, 36.19) * mm, "end": v(115.94, 35.25) * mm});
            skLineSegment(sketch, "E249", {"start": v(115.94, 36.19) * mm, "end": v(116.42, 35.92) * mm});
            skLineSegment(sketch, "E250", {"start": v(116.42, 35.92) * mm, "end": v(116.42, 34.98) * mm});
            skLineSegment(sketch, "E251.0", {"start": v(113.83, 36.43) * mm, "end": v(113.83, 37.08) * mm});
            skLineSegment(sketch, "E251.1", {"start": v(113.83, 35.63) * mm, "end": v(113.83, 36.43) * mm});
            skLineSegment(sketch, "E251.2", {"start": v(112.99, 36.1) * mm, "end": v(113.83, 35.63) * mm});
            skLineSegment(sketch, "E252", {"start": v(113.83, 37.08) * mm, "end": v(112.99, 37.57) * mm});
            skLineSegment(sketch, "E253", {"start": v(112.99, 36.1) * mm, "end": v(112.99, 37.57) * mm});
            skPoint(sketch, "E254.orphan", {"position": v(112.99, 37.57) * mm});
            skPoint(sketch, "E255.orphan", {"position": v(113.83, 37.73) * mm});
            skLineSegment(sketch, "E256.left", {"start": v(116.21, 31.47) * mm, "end": v(116.21, 30.7) * mm});
            skLineSegment(sketch, "E256.right", {"start": v(116.8, 31.49) * mm, "end": v(116.8, 30.38) * mm});
            skLineSegment(sketch, "E257", {"start": v(116.8, 30.38) * mm, "end": v(116.21, 30.7) * mm});
            skLineSegment(sketch, "E258", {"start": v(116.21, 31.47) * mm, "end": v(116.21, 31.82) * mm});
            skLineSegment(sketch, "E259", {"start": v(116.8, 31.49) * mm, "end": v(116.21, 31.82) * mm});
            skLineSegment(sketch, "E260.0", {"start": v(115.98, 27.33) * mm, "end": v(113.82, 28.54) * mm});
            skLineSegment(sketch, "E261.0", {"start": v(113.82, 27.8) * mm, "end": v(115.98, 26.6) * mm});
            skLineSegment(sketch, "E262", {"start": v(115.98, 27.33) * mm, "end": v(115.98, 26.6) * mm});
            skLineSegment(sketch, "E263", {"start": v(113.82, 27.8) * mm, "end": v(113.82, 28.54) * mm});
            skLineSegment(sketch, "E264", {"start": v(117.64, 23.58) * mm, "end": v(117.64, 20.25) * mm});
            skLineSegment(sketch, "E265.0", {"start": v(115.49, 22.39) * mm, "end": v(116.39, 21.89) * mm});
            skLineSegment(sketch, "E265.1", {"start": v(115.49, 23.8) * mm, "end": v(115.49, 22.39) * mm});
            skLineSegment(sketch, "E266", {"start": v(116.39, 21.89) * mm, "end": v(116.39, 23.3) * mm});
            skLineSegment(sketch, "E267", {"start": v(116.39, 23.3) * mm, "end": v(115.49, 23.8) * mm});
            skLineSegment(sketch, "E268.bottom", {"start": v(114.81, 49.92) * mm, "end": v(115.42, 49.92) * mm});
            skLineSegment(sketch, "E268.top", {"start": v(114.81, 38.68) * mm, "end": v(115.42, 38.68) * mm});
            skLineSegment(sketch, "E268.left", {"start": v(114.81, 49.92) * mm, "end": v(114.81, 38.68) * mm});
            skLineSegment(sketch, "E268.right", {"start": v(115.42, 49.92) * mm, "end": v(115.42, 38.68) * mm});
            skLineSegment(sketch, "E269.bottom", {"start": v(114.42, 11.78) * mm, "end": v(115.1, 11.78) * mm});
            skLineSegment(sketch, "E269.top", {"start": v(114.42, -15.06) * mm, "end": v(115.1, -15.06) * mm});
            skLineSegment(sketch, "E269.left", {"start": v(114.42, 11.78) * mm, "end": v(114.42, -15.06) * mm});
            skLineSegment(sketch, "E269.right", {"start": v(115.1, 11.78) * mm, "end": v(115.1, -15.06) * mm});
            skLineSegment(sketch, "E270", {"start": v(113.16, 15.42) * mm, "end": v(114.98, 14.4) * mm});
            skLineSegment(sketch, "E271", {"start": v(115.83, 14.34) * mm, "end": v(115.83, 13.93) * mm});
            skLineSegment(sketch, "E272.trimOffspring", {"start": v(115.83, 13.93) * mm, "end": v(117.64, 12.92) * mm});
            skPoint(sketch, "E273.orphan", {"position": v(117.64, 41.22) * mm});
            skLineSegment(sketch, "E274.trimOffspring", {"start": v(117.64, 19.4) * mm, "end": v(117.64, 18.74) * mm});
            skLineSegment(sketch, "E275.trimOffspring", {"start": v(117.64, 27.46) * mm, "end": v(117.64, 20.25) * mm});
            skLineSegment(sketch, "E276.trimOffspring", {"start": v(117.64, 17.46) * mm, "end": v(117.64, 16.51) * mm});
            skLineSegment(sketch, "E277.trimOffspring", {"start": v(117.64, 15.56) * mm, "end": v(117.64, 14.78) * mm});
            skLineSegment(sketch, "E278.trimOffspring", {"start": v(117.64, 13.33) * mm, "end": v(117.64, 11.93) * mm});
            skLineSegment(sketch, "E279.trimOffspring", {"start": v(112.56, 20.3) * mm, "end": v(112.56, 19.35) * mm});
            skLineSegment(sketch, "E280.trimOffspring", {"start": v(112.56, 31.87) * mm, "end": v(112.56, 30.75) * mm});
            skLineSegment(sketch, "E281.trimOffspring", {"start": v(112.56, 34.62) * mm, "end": v(112.56, 33.56) * mm});
            skPoint(sketch, "E282.orphan", {"position": v(112.56, 41.11) * mm});
            skSolve(sketch);
        }
        {
            var Q0;
            Q0=makeQuery(id+"F7.imprint","IMPRINT",FACE,{"disambiguationData":[TD([[makeQuery(id+"F7.imprint","IMPRINT",EDGE,{"derivedFrom":sQuery(id+"F7.wireOp",EDGE,"E199")}),-1.0]])]});
            var Q1;
            Q1=makeQuery(id+"F7.imprint","IMPRINT",FACE,{"disambiguationData":[TD([[makeQuery(id+"F7.imprint","IMPRINT",EDGE,{"derivedFrom":sQuery(id+"F7.wireOp",EDGE,"E248.0")}),1.0]])]});
            var Q2;
            Q2=makeQuery(id+"F7.imprint","IMPRINT",FACE,{"disambiguationData":[TD([[makeQuery(id+"F7.imprint","IMPRINT",EDGE,{"derivedFrom":sQuery(id+"F7.wireOp",EDGE,"E251.0")}),1.0]])]});
            var Q3;
            Q3=makeQuery(id+"F7.imprint","IMPRINT",FACE,{"disambiguationData":[TD([[makeQuery(id+"F7.imprint","IMPRINT",EDGE,{"derivedFrom":sQuery(id+"F7.wireOp",EDGE,"E256.left")}),1.0]])]});
            var Q4;
            Q4=makeQuery(id+"F7.imprint","IMPRINT",FACE,{"disambiguationData":[TD([[makeQuery(id+"F7.imprint","IMPRINT",EDGE,{"derivedFrom":sQuery(id+"F7.wireOp",EDGE,"E260.0")}),1.0]])]});
            var Q5;
            Q5=makeQuery(id+"F7.imprint","IMPRINT",FACE,{"disambiguationData":[TD([[makeQuery(id+"F7.imprint","IMPRINT",EDGE,{"derivedFrom":sQuery(id+"F7.wireOp",EDGE,"E265.0")}),1.0]])]});
            extrude(context, id + "F8", {"entities" : qUnion([Q0, Q1, Q2, Q3, Q4, Q5]), "operationType" : NewBodyOperationType.REMOVE, "oppositeDirection" : true, "depth" : 1.27 * mm});
        }
    });
